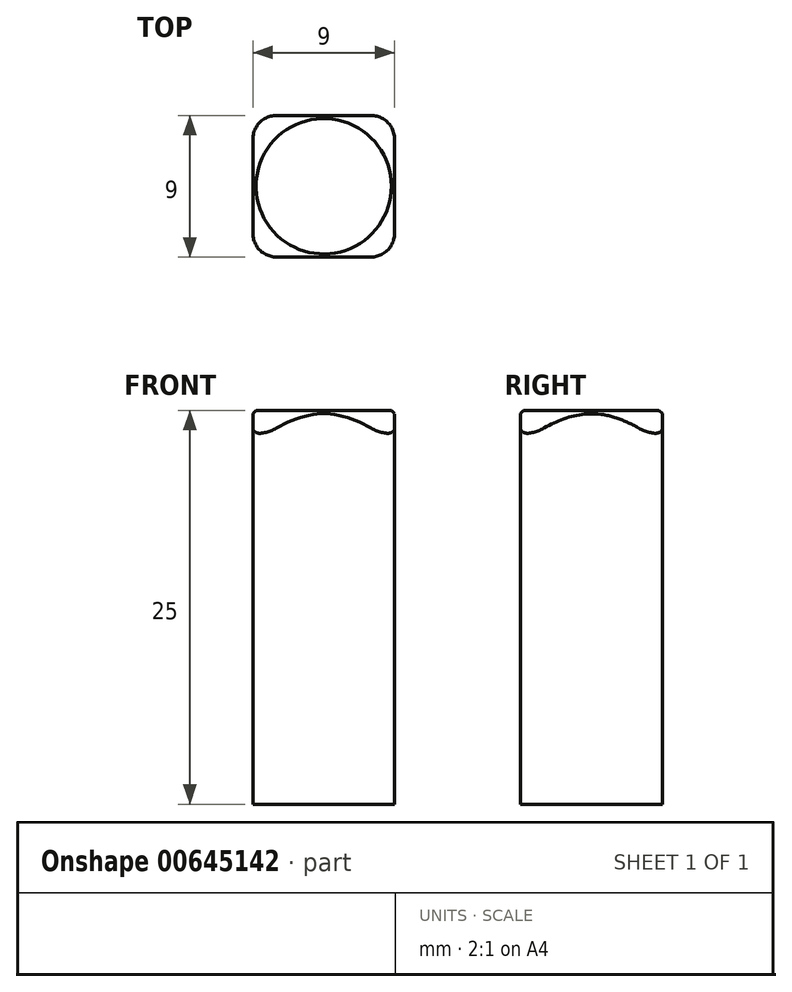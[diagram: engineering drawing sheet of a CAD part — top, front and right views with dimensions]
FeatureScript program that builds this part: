
annotation { "Feature Type Name" : "Feature", "Feature Type Description" : "" }
export const myFeature = defineFeature(function(context is Context, id is Id, definition is map)
    precondition{}
    {
        {
            var Q0;
            Q0=qCreatedBy(makeId("Top.planeOp"),FACE);
            var sketch = newSketch(context, id + "F0", { "sketchPlane" : qUnion([Q0])});
            skLineSegment(sketch, "E0.bottom", {"start": v(4.5, -4.5) * mm, "end": v(-4.5, -4.5) * mm});
            skLineSegment(sketch, "E0.top", {"start": v(4.5, 4.5) * mm, "end": v(-4.5, 4.5) * mm});
            skLineSegment(sketch, "E0.left", {"start": v(4.5, -4.5) * mm, "end": v(4.5, 4.5) * mm});
            skLineSegment(sketch, "E0.right", {"start": v(-4.5, -4.5) * mm, "end": v(-4.5, 4.5) * mm});
            skPoint(sketch, "E0.middle", {"position": v(0, 0) * mm});
            skCircle(sketch, "E1", {"center": v(0, 0) * mm, "radius": 4.3 * mm});
            skSolve(sketch);
        }
        {
            var Q0;
            Q0=makeQuery(id+"F0.imprint","IMPRINT",FACE,{"disambiguationData":[TD([[makeQuery(id+"F0.imprint","IMPRINT",EDGE,{"derivedFrom":sQuery(id+"F0.wireOp",EDGE,"E0.bottom")}),-1.0]])]});
            var Q1;
            Q1=makeQuery(id+"F0.imprint","IMPRINT",FACE,{"disambiguationData":[TD([[makeQuery(id+"F0.imprint","IMPRINT",EDGE,{"derivedFrom":sQuery(id+"F0.wireOp",EDGE,"E1")}),1.0]])]});
            var Q2;
            {var subQ0=sQuery(id+"F0.wireOp",EDGE,"E1");var subQ1=sQuery(id+"F0.wireOp",EDGE,"E0.top");var subQ2=makeQuery(id+"F0.imprint","INTERSECT",VERTEX,{"derivedFrom":[subQ1,subQ0]});Q2=makeQuery(id+"F0.imprint","IMPRINT",FACE,{"disambiguationData":[TD([[makeQuery(id+"F0.imprint","IMPRINT",EDGE,{"disambiguationData":[TD([[subQ2,1.0]])],"derivedFrom":subQ1}),1.0]])]});}
            var Q3;
            {var subQ0=sQuery(id+"F0.wireOp",EDGE,"E1");var subQ1=sQuery(id+"F0.wireOp",EDGE,"E0.top");var subQ2=makeQuery(id+"F0.imprint","INTERSECT",VERTEX,{"derivedFrom":[subQ1,subQ0]});Q3=makeQuery(id+"F0.imprint","IMPRINT",FACE,{"disambiguationData":[TD([[makeQuery(id+"F0.imprint","IMPRINT",EDGE,{"disambiguationData":[TD([[subQ2,-1.0]])],"derivedFrom":subQ1}),1.0]])]});}
            extrude(context, id + "F1", {"entities" : qUnion([Q0, Q1, Q2, Q3]), "oppositeDirection" : true, "depth" : 25 * mm, "offsetDistance" : 25 * mm});
        }
        {
            var Q0;
            Q0=makeQuery(id+"F0.imprint","IMPRINT",FACE,{"disambiguationData":[TD([[makeQuery(id+"F0.imprint","IMPRINT",EDGE,{"derivedFrom":sQuery(id+"F0.wireOp",EDGE,"E0.bottom")}),-1.0]])]});
            var Q1;
            {var subQ0=sQuery(id+"F0.wireOp",EDGE,"E1");var subQ1=sQuery(id+"F0.wireOp",EDGE,"E0.top");var subQ2=makeQuery(id+"F0.imprint","INTERSECT",VERTEX,{"derivedFrom":[subQ1,subQ0]});Q1=makeQuery(id+"F0.imprint","IMPRINT",FACE,{"disambiguationData":[TD([[makeQuery(id+"F0.imprint","IMPRINT",EDGE,{"disambiguationData":[TD([[subQ2,1.0]])],"derivedFrom":subQ1}),1.0]])]});}
            var Q2;
            {var subQ0=sQuery(id+"F0.wireOp",EDGE,"E1");var subQ1=sQuery(id+"F0.wireOp",EDGE,"E0.top");var subQ2=makeQuery(id+"F0.imprint","INTERSECT",VERTEX,{"derivedFrom":[subQ1,subQ0]});Q2=makeQuery(id+"F0.imprint","IMPRINT",FACE,{"disambiguationData":[TD([[makeQuery(id+"F0.imprint","IMPRINT",EDGE,{"disambiguationData":[TD([[subQ2,-1.0]])],"derivedFrom":subQ1}),1.0]])]});}
            extrude(context, id + "F2", {"entities" : qUnion([Q0, Q1, Q2]), "operationType" : NewBodyOperationType.REMOVE, "oppositeDirection" : true, "depth" : 2 * mm, "offsetDistance" : 25 * mm});
        }
        {
            var Q0;
            Q0=makeQuery(id+"F1.opExtrude","SWEPT_EDGE",EDGE,{"disambiguationData":[OSD([sQuery(id+"F0.wireOp",EDGE,"E0.bottom"),sQuery(id+"F0.wireOp",EDGE,"E0.left")])]});
            var Q1;
            Q1=makeQuery(id+"F1.opExtrude","SWEPT_EDGE",EDGE,{"disambiguationData":[OSD([sQuery(id+"F0.wireOp",EDGE,"E0.top"),sQuery(id+"F0.wireOp",EDGE,"E0.left")])]});
            var Q2;
            Q2=makeQuery(id+"F1.opExtrude","SWEPT_EDGE",EDGE,{"disambiguationData":[OSD([sQuery(id+"F0.wireOp",EDGE,"E0.top"),sQuery(id+"F0.wireOp",EDGE,"E0.right")])]});
            var Q3;
            Q3=makeQuery(id+"F1.opExtrude","SWEPT_EDGE",EDGE,{"disambiguationData":[OSD([sQuery(id+"F0.wireOp",EDGE,"E0.bottom"),sQuery(id+"F0.wireOp",EDGE,"E0.right")])]});
            fillet(context, id + "F3", {"entities" : qUnion([Q0, Q1, Q2, Q3]), "tangentPropagation" : true, "radius" : 1.5 * mm, "defaultsChanged" : true, "vertexSettings" : [], "allowEdgeOverflow" : false});
        }
        {
            var Q0;
            Q0=makeQuery(id+"F2.boolean.opBoolean","COPY",EDGE,{"derivedFrom":makeQuery(id+"F2.opExtrude","CAP_EDGE",EDGE,{"disambiguationData":[OSD([sQuery(id+"F0.wireOp",EDGE,"E1")])],"isStart":false})});
            chamfer(context, id + "F4", {"entities" : qUnion([Q0]), "chamferType" : ChamferType.TWO_OFFSETS, "width1" : 2 * mm, "oppositeDirection" : false, "width2" : 2 * mm, "tangentPropagation" : true});
        }
    });
